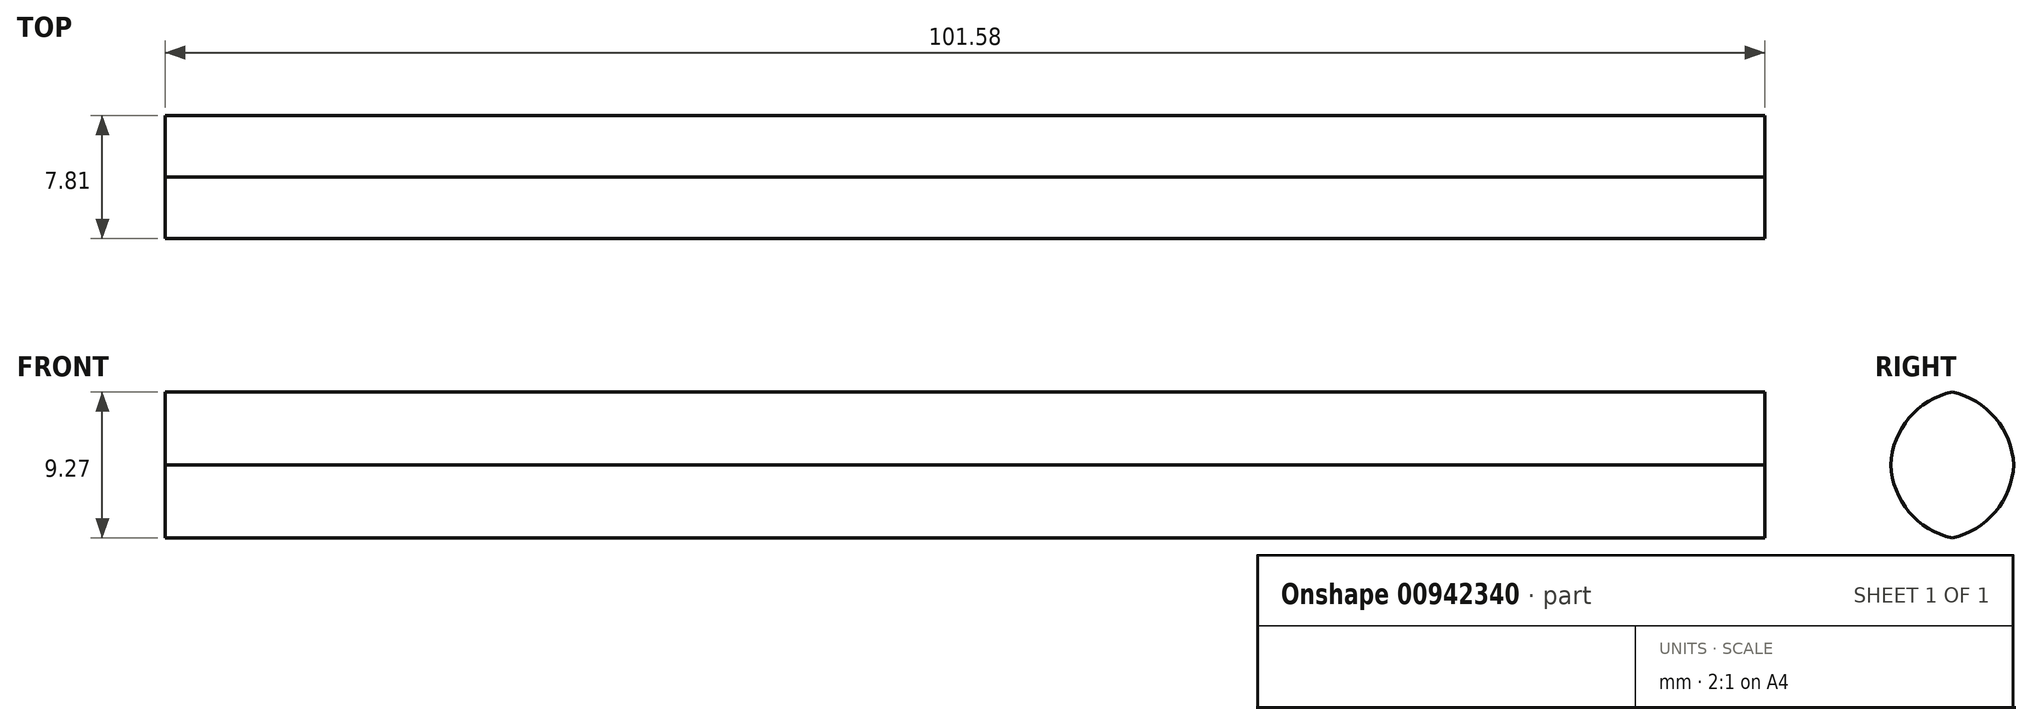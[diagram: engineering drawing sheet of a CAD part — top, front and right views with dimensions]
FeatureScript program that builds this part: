
annotation { "Feature Type Name" : "Feature", "Feature Type Description" : "" }
export const myFeature = defineFeature(function(context is Context, id is Id, definition is map)
    precondition{}
    {
        {
            var Q0;
            Q0=qCreatedBy(makeId("Right.planeOp"),FACE);
            var sketch = newSketch(context, id + "F0", { "sketchPlane" : qUnion([Q0])});
            skLineSegment(sketch, "E0.bottom", {"start": v(-26.42, 39.56) * mm, "end": v(-18.6, 39.56) * mm});
            skLineSegment(sketch, "E0.top", {"start": v(-26.42, 30.05) * mm, "end": v(-18.6, 30.05) * mm});
            skLineSegment(sketch, "E0.left", {"start": v(-26.42, 39.56) * mm, "end": v(-26.42, 30.05) * mm});
            skLineSegment(sketch, "E0.right", {"start": v(-18.6, 39.56) * mm, "end": v(-18.6, 30.05) * mm});
            skSolve(sketch);
        }
        {
            var Q0;
            Q0=makeQuery(id+"F0.imprint","IMPRINT",FACE,{"disambiguationData":[TD([[makeQuery(id+"F0.imprint","IMPRINT",EDGE,{"derivedFrom":sQuery(id+"F0.wireOp",EDGE,"E0.bottom")}),-1.0]])]});
            var sketch = newSketch(context, id + "F1", { "sketchPlane" : qUnion([Q0])});
            skLineSegment(sketch, "E1.0", {"start": v(-26.42, 39.56) * mm, "end": v(-26.42, 30.05) * mm});
            skLineSegment(sketch, "E2.0", {"start": v(-18.6, 39.56) * mm, "end": v(-18.6, 30.05) * mm});
            skLineSegment(sketch, "E3.0", {"start": v(-26.42, 39.56) * mm, "end": v(-18.6, 39.56) * mm});
            skLineSegment(sketch, "E4.0", {"start": v(-26.42, 30.05) * mm, "end": v(-18.6, 30.05) * mm});
            skSolve(sketch);
        }
        {
            var Q0;
            Q0=makeQuery(id+"F0.imprint","IMPRINT",FACE,{"disambiguationData":[TD([[makeQuery(id+"F0.imprint","IMPRINT",EDGE,{"derivedFrom":sQuery(id+"F0.wireOp",EDGE,"E0.bottom")}),-1.0]])]});
            extrude(context, id + "F2", {"entities" : qUnion([Q0]), "depth" : 25 * mm, "offsetDistance" : 25 * mm});
        }
        {
            var Q0;
            Q0=makeQuery(id+"F2.opExtrude","CAP_FACE",FACE,{"disambiguationData":[OSD([sQuery(id+"F0.wireOp",EDGE,"E0.bottom"),sQuery(id+"F0.wireOp",EDGE,"E0.top"),sQuery(id+"F0.wireOp",EDGE,"E0.left"),sQuery(id+"F0.wireOp",EDGE,"E0.right")])],"isStart":false});
            extrude(context, id + "F3", {"entities" : qUnion([Q0]), "operationType" : NewBodyOperationType.ADD, "depth" : 25 * mm, "offsetDistance" : 25 * mm});
        }
        {
            var Q0;
            Q0=makeQuery(id+"F1.imprint","IMPRINT",FACE,{"disambiguationData":[TD([[makeQuery(id+"F1.imprint","IMPRINT",EDGE,{"derivedFrom":sQuery(id+"F1.wireOp",EDGE,"E1.0")}),1.0]])]});
            extrude(context, id + "F4", {"entities" : qUnion([Q0]), "operationType" : NewBodyOperationType.ADD, "oppositeDirection" : true, "depth" : 51.58 * mm, "offsetDistance" : 25 * mm});
        }
        {
            var Q1;
            Q1=makeQuery(id+"F3.opExtrude","CAP_FACE",FACE,{"disambiguationData":[OSD([sQuery(id+"F0.wireOp",EDGE,"E0.bottom"),sQuery(id+"F0.wireOp",EDGE,"E0.top"),sQuery(id+"F0.wireOp",EDGE,"E0.left"),sQuery(id+"F0.wireOp",EDGE,"E0.right")])],"isStart":false});
            var Q2;
            Q2=makeQuery(id+"F4.opExtrude","CAP_FACE",FACE,{"disambiguationData":[OSD([sQuery(id+"F1.wireOp",EDGE,"E1.0"),sQuery(id+"F1.wireOp",EDGE,"E2.0"),sQuery(id+"F1.wireOp",EDGE,"E3.0"),sQuery(id+"F1.wireOp",EDGE,"E4.0")])],"isStart":false});
            loft(context, id + "F5", {"operationType" : NewBodyOperationType.ADD, "sheetProfilesArray" : [{ "sheetProfileEntities" : qUnion([Q1]) }, { "sheetProfileEntities" : qUnion([Q2]) }]});
        }
        {
            var Q0;
            {var subQ0=sQuery(id+"F0.wireOp",EDGE,"E0.left");var subQ1=sQuery(id+"F0.wireOp",EDGE,"E0.bottom");Q0=makeQuery(id+"F4.boolean.opBoolean","MERGE",EDGE,{"derivedFrom":[makeQuery(id+"F3.boolean.opBoolean","MERGE",EDGE,{"derivedFrom":[makeQuery(id+"F2.opExtrude","SWEPT_EDGE",EDGE,{"disambiguationData":[OSD([subQ1,subQ0])]}),makeQuery(id+"F3.opExtrude","SWEPT_EDGE",EDGE,{"disambiguationData":[OSD([subQ1,subQ0])]})]}),makeQuery(id+"F4.opExtrude","SWEPT_EDGE",EDGE,{"disambiguationData":[OSD([sQuery(id+"F1.wireOp",EDGE,"E1.0"),sQuery(id+"F1.wireOp",EDGE,"E3.0")])]})]});}
            var Q1;
            {var subQ0=sQuery(id+"F0.wireOp",EDGE,"E0.right");var subQ1=sQuery(id+"F0.wireOp",EDGE,"E0.bottom");Q1=makeQuery(id+"F4.boolean.opBoolean","MERGE",EDGE,{"derivedFrom":[makeQuery(id+"F3.boolean.opBoolean","MERGE",EDGE,{"derivedFrom":[makeQuery(id+"F2.opExtrude","SWEPT_EDGE",EDGE,{"disambiguationData":[OSD([subQ1,subQ0])]}),makeQuery(id+"F3.opExtrude","SWEPT_EDGE",EDGE,{"disambiguationData":[OSD([subQ1,subQ0])]})]}),makeQuery(id+"F4.opExtrude","SWEPT_EDGE",EDGE,{"disambiguationData":[OSD([sQuery(id+"F1.wireOp",EDGE,"E2.0"),sQuery(id+"F1.wireOp",EDGE,"E3.0")])]})]});}
            var Q2;
            {var subQ0=sQuery(id+"F0.wireOp",EDGE,"E0.left");var subQ1=sQuery(id+"F0.wireOp",EDGE,"E0.top");Q2=makeQuery(id+"F4.boolean.opBoolean","MERGE",EDGE,{"derivedFrom":[makeQuery(id+"F3.boolean.opBoolean","MERGE",EDGE,{"derivedFrom":[makeQuery(id+"F2.opExtrude","SWEPT_EDGE",EDGE,{"disambiguationData":[OSD([subQ1,subQ0])]}),makeQuery(id+"F3.opExtrude","SWEPT_EDGE",EDGE,{"disambiguationData":[OSD([subQ1,subQ0])]})]}),makeQuery(id+"F4.opExtrude","SWEPT_EDGE",EDGE,{"disambiguationData":[OSD([sQuery(id+"F1.wireOp",EDGE,"E1.0"),sQuery(id+"F1.wireOp",EDGE,"E4.0")])]})]});}
            var Q3;
            {var subQ0=sQuery(id+"F0.wireOp",EDGE,"E0.right");var subQ1=sQuery(id+"F0.wireOp",EDGE,"E0.top");Q3=makeQuery(id+"F4.boolean.opBoolean","MERGE",EDGE,{"derivedFrom":[makeQuery(id+"F3.boolean.opBoolean","MERGE",EDGE,{"derivedFrom":[makeQuery(id+"F2.opExtrude","SWEPT_EDGE",EDGE,{"disambiguationData":[OSD([subQ1,subQ0])]}),makeQuery(id+"F3.opExtrude","SWEPT_EDGE",EDGE,{"disambiguationData":[OSD([subQ1,subQ0])]})]}),makeQuery(id+"F4.opExtrude","SWEPT_EDGE",EDGE,{"disambiguationData":[OSD([sQuery(id+"F1.wireOp",EDGE,"E2.0"),sQuery(id+"F1.wireOp",EDGE,"E4.0")])]})]});}
            fillet(context, id + "F6", {"entities" : qUnion([Q0, Q1, Q2, Q3]), "radius" : 5 * mm, "tangentPropagation" : true, "allowEdgeOverflow" : false});
        }
    });
